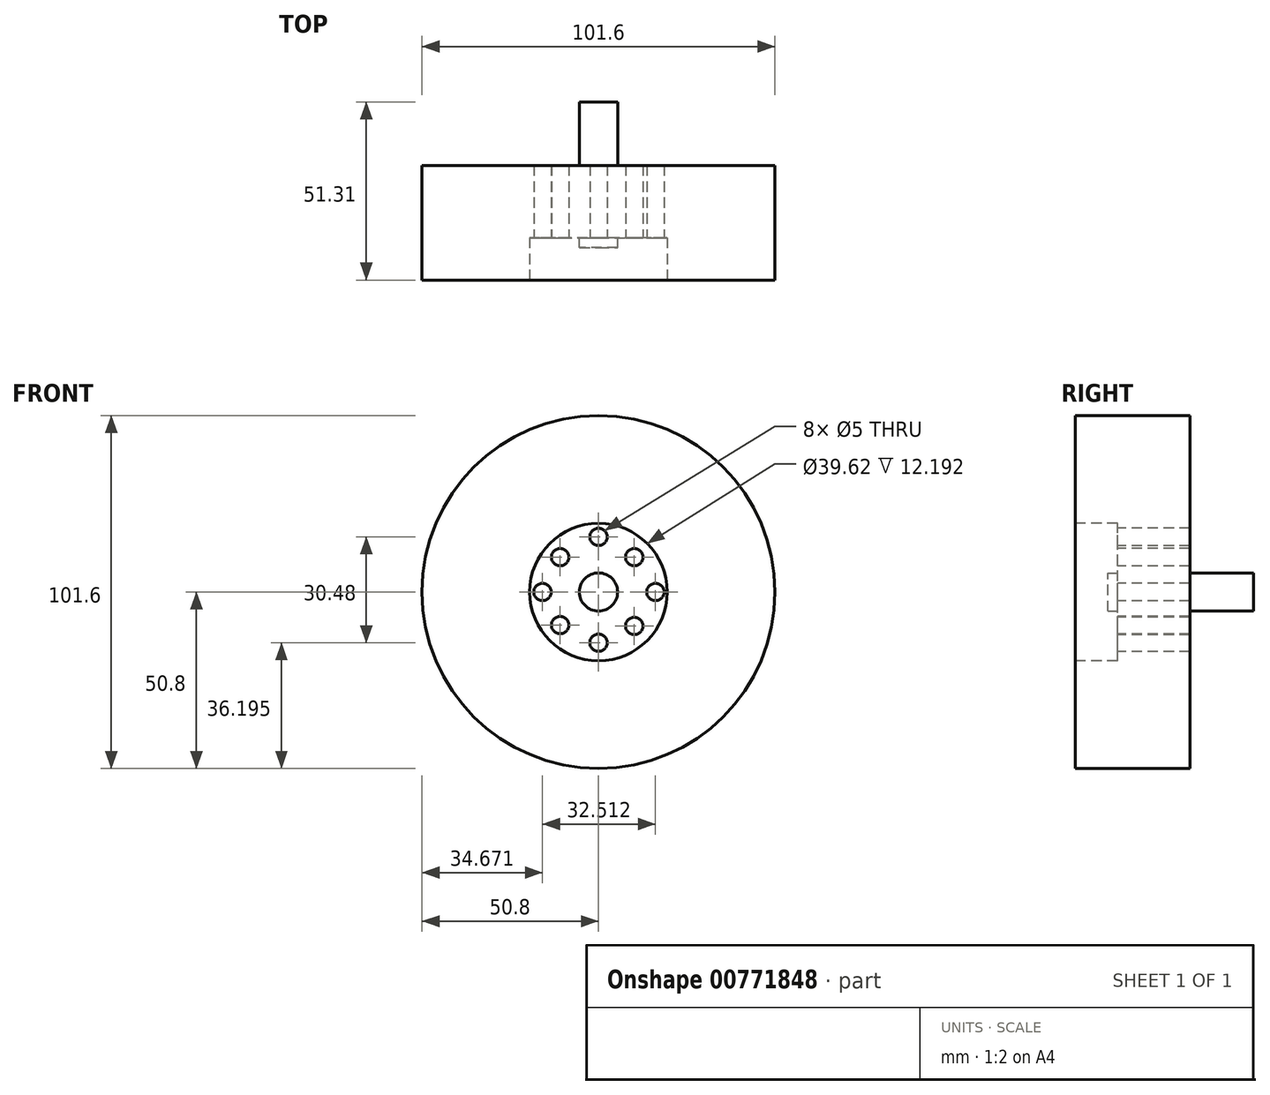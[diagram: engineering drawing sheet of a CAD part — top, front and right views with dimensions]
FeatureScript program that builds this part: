
annotation { "Feature Type Name" : "Feature", "Feature Type Description" : "" }
export const myFeature = defineFeature(function(context is Context, id is Id, definition is map)
    precondition{}
    {
        {
            var Q0;
            Q0=qCreatedBy(makeId("Front.planeOp"),FACE);
            var sketch = newSketch(context, id + "F0", { "sketchPlane" : qUnion([Q0])});
            skCircle(sketch, "E0", {"center": v(0, 0) * mm, "radius": 50.8 * mm});
            skSolve(sketch);
        }
        {
            var Q0;
            Q0=makeQuery(id+"F0.imprint","IMPRINT",FACE,{"disambiguationData":[TD([[makeQuery(id+"F0.imprint","IMPRINT",EDGE,{"derivedFrom":sQuery(id+"F0.wireOp",EDGE,"E0")}),1.0]])]});
            extrude(context, id + "F1", {"entities" : qUnion([Q0]), "depth" : 33.02 * mm, "offsetDistance" : 25.4 * mm});
        }
        {
            var Q0;
            Q0=makeQuery(id+"F1.opExtrude","CAP_FACE",FACE,{"disambiguationData":[OSD([sQuery(id+"F0.wireOp",EDGE,"E0")])],"isStart":false});
            var sketch = newSketch(context, id + "F2", { "sketchPlane" : qUnion([Q0])});
            skCircle(sketch, "E1", {"center": v(0, 0) * mm, "radius": 19.81 * mm});
            skSolve(sketch);
        }
        {
            var Q0;
            Q0=makeQuery(id+"F2.imprint","IMPRINT",FACE,{"disambiguationData":[TD([[makeQuery(id+"F2.imprint","IMPRINT",EDGE,{"derivedFrom":sQuery(id+"F2.wireOp",EDGE,"E1")}),1.0]])]});
            extrude(context, id + "F3", {"entities" : qUnion([Q0]), "operationType" : NewBodyOperationType.REMOVE, "oppositeDirection" : true, "depth" : 12.2 * mm, "offsetDistance" : 25.4 * mm});
        }
        {
            var Q0;
            Q0=makeQuery(id+"F3.boolean.opBoolean","COPY",FACE,{"derivedFrom":makeQuery(id+"F3.opExtrude","CAP_FACE",FACE,{"disambiguationData":[OSD([sQuery(id+"F2.wireOp",EDGE,"E1")])],"isStart":false})});
            var sketch = newSketch(context, id + "F4", { "sketchPlane" : qUnion([Q0])});
            skCircle(sketch, "E2", {"center": v(0, 0) * mm, "radius": 5.5 * mm});
            skSolve(sketch);
        }
        {
            var Q0;
            Q0=makeQuery(id+"F4.imprint","IMPRINT",FACE,{"disambiguationData":[TD([[makeQuery(id+"F4.imprint","IMPRINT",EDGE,{"derivedFrom":sQuery(id+"F4.wireOp",EDGE,"E2")}),1.0]])]});
            extrude(context, id + "F5", {"entities" : qUnion([Q0]), "operationType" : NewBodyOperationType.ADD, "depth" : 2.8 * mm, "offsetDistance" : 25.4 * mm});
        }
        {
            var Q0;
            Q0=makeQuery(id+"F3.boolean.opBoolean","COPY",FACE,{"derivedFrom":makeQuery(id+"F3.opExtrude","CAP_FACE",FACE,{"disambiguationData":[OSD([sQuery(id+"F2.wireOp",EDGE,"E1")])],"isStart":false})});
            var sketch = newSketch(context, id + "F6", { "sketchPlane" : qUnion([Q0])});
            skCircle(sketch, "E3", {"center": v(0, -14.6) * mm, "radius": 2.5 * mm});
            skCircle(sketch, "E4", {"center": v(0, 15.88) * mm, "radius": 2.5 * mm});
            skCircle(sketch, "E5", {"center": v(-16.13, 0) * mm, "radius": 2.5 * mm});
            skCircle(sketch, "E6", {"center": v(16.38, 0) * mm, "radius": 2.5 * mm});
            skCircle(sketch, "E7", {"center": v(-11.05, 10.03) * mm, "radius": 2.5 * mm});
            skCircle(sketch, "E8", {"center": v(-11.05, -9.53) * mm, "radius": 2.5 * mm});
            skCircle(sketch, "E9", {"center": v(10.29, -9.78) * mm, "radius": 2.5 * mm});
            skCircle(sketch, "E10", {"center": v(10.29, 10.03) * mm, "radius": 2.5 * mm});
            skSolve(sketch);
        }
        {
            var Q0;
            Q0=makeQuery(id+"F6.imprint","IMPRINT",FACE,{"disambiguationData":[TD([[makeQuery(id+"F6.imprint","IMPRINT",EDGE,{"derivedFrom":sQuery(id+"F6.wireOp",EDGE,"E4")}),1.0]])]});
            var Q1;
            Q1=makeQuery(id+"F6.imprint","IMPRINT",FACE,{"disambiguationData":[TD([[makeQuery(id+"F6.imprint","IMPRINT",EDGE,{"derivedFrom":sQuery(id+"F6.wireOp",EDGE,"E7")}),1.0]])]});
            var Q2;
            Q2=makeQuery(id+"F6.imprint","IMPRINT",FACE,{"disambiguationData":[TD([[makeQuery(id+"F6.imprint","IMPRINT",EDGE,{"derivedFrom":sQuery(id+"F6.wireOp",EDGE,"E5")}),1.0]])]});
            var Q3;
            Q3=makeQuery(id+"F6.imprint","IMPRINT",FACE,{"disambiguationData":[TD([[makeQuery(id+"F6.imprint","IMPRINT",EDGE,{"derivedFrom":sQuery(id+"F6.wireOp",EDGE,"E8")}),1.0]])]});
            var Q4;
            Q4=makeQuery(id+"F6.imprint","IMPRINT",FACE,{"disambiguationData":[TD([[makeQuery(id+"F6.imprint","IMPRINT",EDGE,{"derivedFrom":sQuery(id+"F6.wireOp",EDGE,"E3")}),1.0]])]});
            var Q5;
            Q5=makeQuery(id+"F6.imprint","IMPRINT",FACE,{"disambiguationData":[TD([[makeQuery(id+"F6.imprint","IMPRINT",EDGE,{"derivedFrom":sQuery(id+"F6.wireOp",EDGE,"E9")}),1.0]])]});
            var Q6;
            Q6=makeQuery(id+"F6.imprint","IMPRINT",FACE,{"disambiguationData":[TD([[makeQuery(id+"F6.imprint","IMPRINT",EDGE,{"derivedFrom":sQuery(id+"F6.wireOp",EDGE,"E6")}),1.0]])]});
            var Q7;
            Q7=makeQuery(id+"F6.imprint","IMPRINT",FACE,{"disambiguationData":[TD([[makeQuery(id+"F6.imprint","IMPRINT",EDGE,{"derivedFrom":sQuery(id+"F6.wireOp",EDGE,"E10")}),1.0]])]});
            extrude(context, id + "F7", {"entities" : qUnion([Q0, Q1, Q2, Q3, Q4, Q5, Q6, Q7]), "operationType" : NewBodyOperationType.REMOVE, "oppositeDirection" : true, "depth" : 25.4 * mm, "offsetDistance" : 25.4 * mm});
        }
        {
            var Q0;
            Q0=makeQuery(id+"F1.opExtrude","CAP_FACE",FACE,{"disambiguationData":[OSD([sQuery(id+"F0.wireOp",EDGE,"E0")])],"isStart":true});
            var sketch = newSketch(context, id + "F8", { "sketchPlane" : qUnion([Q0])});
            skCircle(sketch, "E11", {"center": v(0, 0) * mm, "radius": 5.5 * mm});
            skSolve(sketch);
        }
        {
            var Q0;
            Q0=makeQuery(id+"F8.imprint","IMPRINT",FACE,{"disambiguationData":[TD([[makeQuery(id+"F8.imprint","IMPRINT",EDGE,{"derivedFrom":sQuery(id+"F8.wireOp",EDGE,"E11")}),1.0]])]});
            extrude(context, id + "F9", {"entities" : qUnion([Q0]), "operationType" : NewBodyOperationType.ADD, "depth" : 18.29 * mm, "offsetDistance" : 25.4 * mm});
        }
    });
